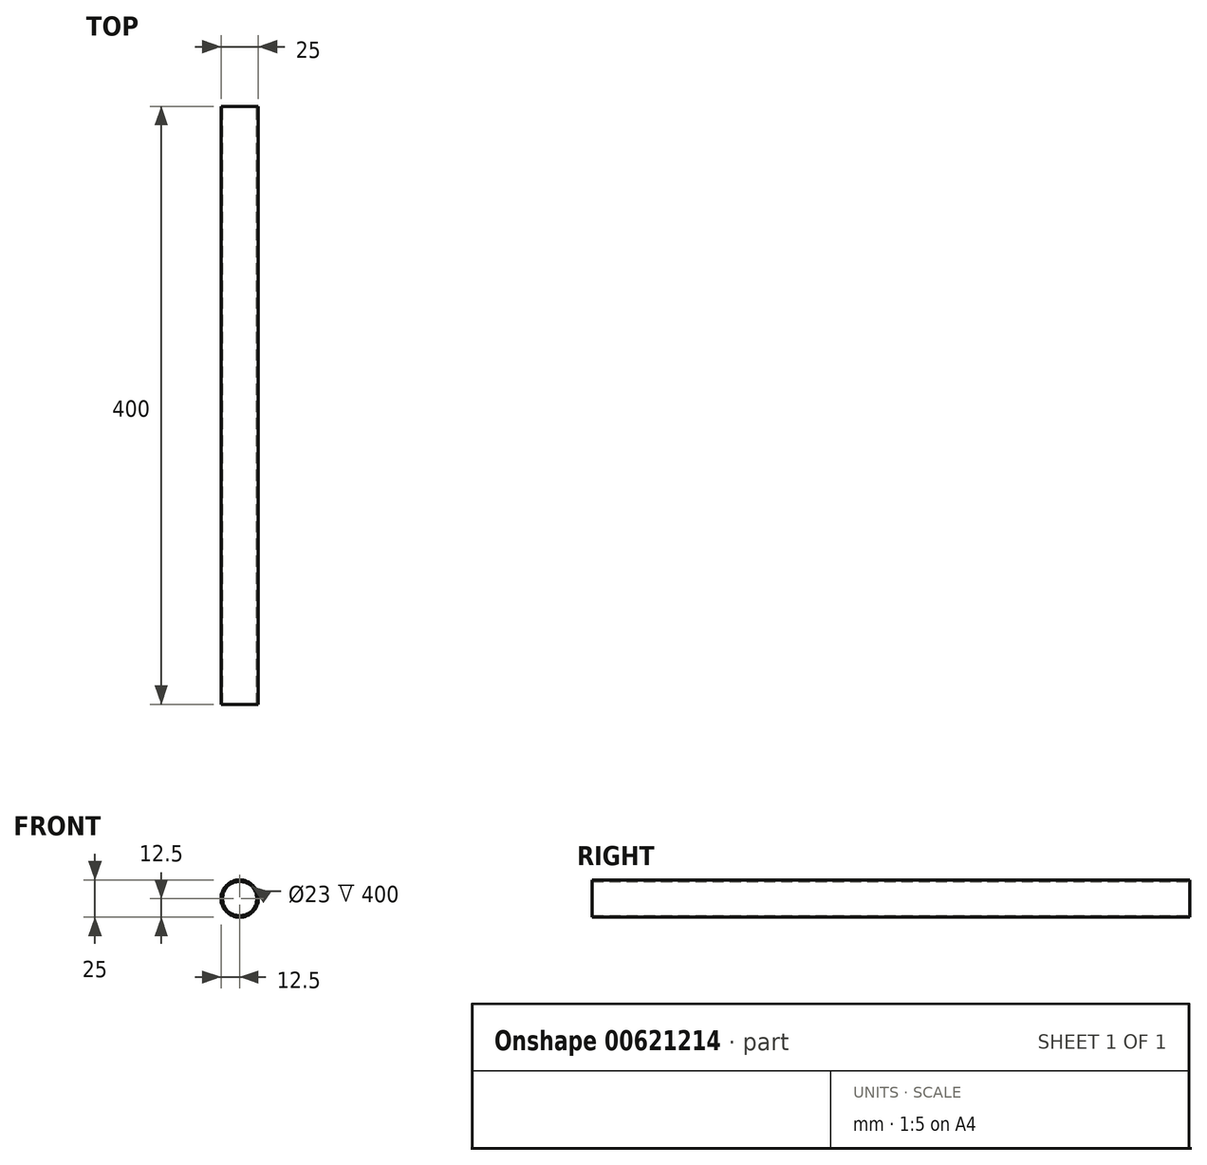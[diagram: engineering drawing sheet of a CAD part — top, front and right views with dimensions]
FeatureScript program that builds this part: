
annotation { "Feature Type Name" : "Feature", "Feature Type Description" : "" }
export const myFeature = defineFeature(function(context is Context, id is Id, definition is map)
    precondition{}
    {
        {
            var Q0;
            Q0=qCreatedBy(makeId("Front.planeOp"),FACE);
            var sketch = newSketch(context, id + "F0", { "sketchPlane" : qUnion([Q0])});
            skCircle(sketch, "E0", {"center": v(0, 0) * mm, "radius": 12.5 * mm});
            skCircle(sketch, "E1", {"center": v(0, 0) * mm, "radius": 11.5 * mm});
            skSolve(sketch);
        }
        {
            var Q0;
            Q0 = qSketchRegion(id + "F0", true);
            extrude(context, id + "F1", {"entities" : qUnion([Q0]), "depth" : 400 * mm, "offsetDistance" : 25 * mm});
        }
    });
